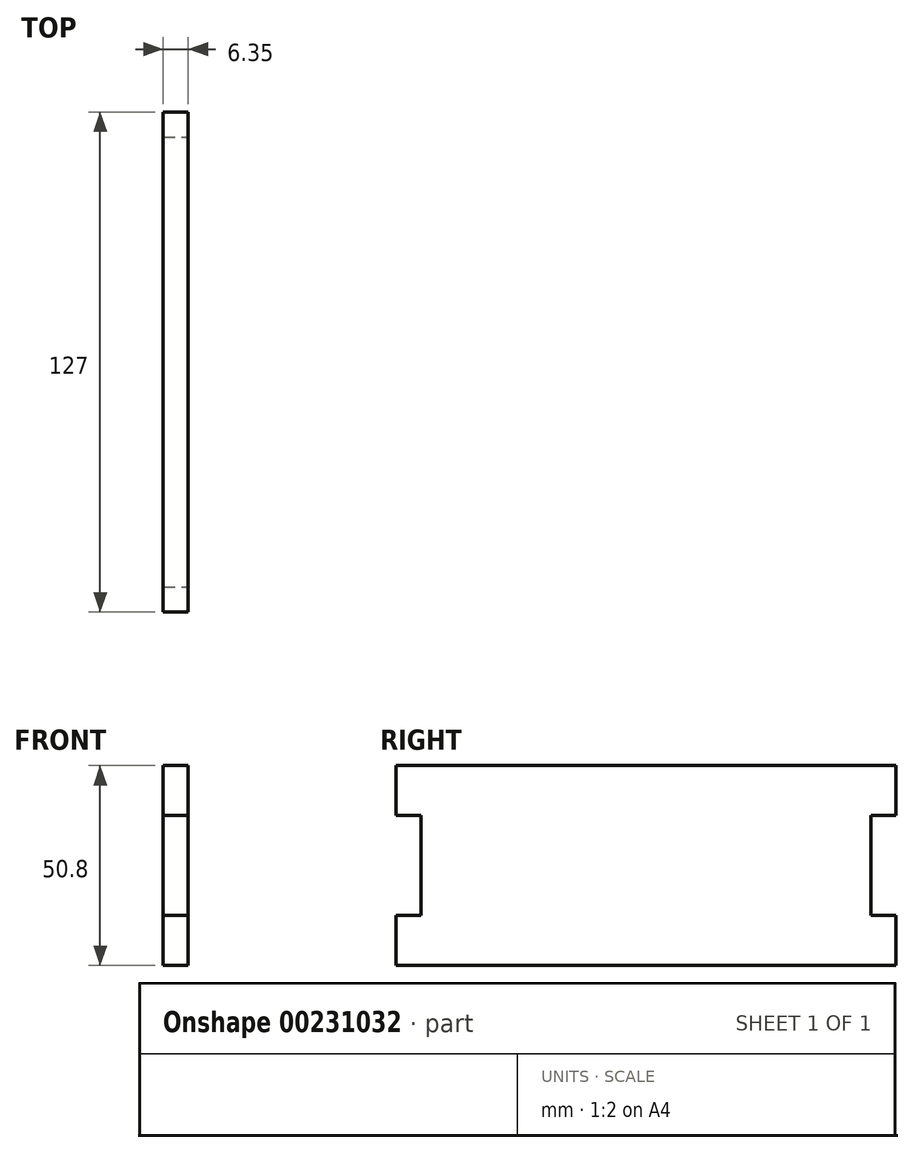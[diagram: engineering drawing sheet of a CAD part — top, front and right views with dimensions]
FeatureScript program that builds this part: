
annotation { "Feature Type Name" : "Feature", "Feature Type Description" : "" }
export const myFeature = defineFeature(function(context is Context, id is Id, definition is map)
    precondition{}
    {
        {
            var Q0;
            Q0=qCreatedBy(makeId("Right.planeOp"),FACE);
            var sketch = newSketch(context, id + "F0", { "sketchPlane" : qUnion([Q0])});
            skLineSegment(sketch, "E0.bottom", {"start": v(63.5, 25.4) * mm, "end": v(-63.5, 25.4) * mm});
            skLineSegment(sketch, "E0.top", {"start": v(63.5, -25.4) * mm, "end": v(-63.5, -25.4) * mm});
            skLineSegment(sketch, "E0.left", {"start": v(63.5, 25.4) * mm, "end": v(63.5, 12.7) * mm});
            skLineSegment(sketch, "E0.right", {"start": v(-63.5, 25.4) * mm, "end": v(-63.5, 12.7) * mm});
            skPoint(sketch, "E0.middle", {"position": v(0, 0) * mm});
            skLineSegment(sketch, "E1.bottom", {"start": v(-63.5, 25.4) * mm, "end": v(-57.15, 25.4) * mm});
            skLineSegment(sketch, "E1.top", {"start": v(-63.5, 19.05) * mm, "end": v(-57.15, 19.05) * mm});
            skLineSegment(sketch, "E1.left", {"start": v(-63.5, 25.4) * mm, "end": v(-63.5, 19.05) * mm});
            skLineSegment(sketch, "E1.right", {"start": v(-57.15, 25.4) * mm, "end": v(-57.15, 19.05) * mm});
            skLineSegment(sketch, "E2.top", {"start": v(-63.5, 12.7) * mm, "end": v(-57.15, 12.7) * mm});
            skLineSegment(sketch, "E2.left", {"start": v(-63.5, 19.05) * mm, "end": v(-63.5, 12.7) * mm});
            skLineSegment(sketch, "E2.right", {"start": v(-57.15, 19.05) * mm, "end": v(-57.15, 12.7) * mm});
            skLineSegment(sketch, "E3.bottom", {"start": v(-63.5, -19.05) * mm, "end": v(-57.15, -19.05) * mm});
            skLineSegment(sketch, "E3.top", {"start": v(-63.5, -25.4) * mm, "end": v(-57.15, -25.4) * mm});
            skLineSegment(sketch, "E3.left", {"start": v(-63.5, -19.05) * mm, "end": v(-63.5, -25.4) * mm});
            skLineSegment(sketch, "E3.right", {"start": v(-57.15, -19.05) * mm, "end": v(-57.15, -25.4) * mm});
            skLineSegment(sketch, "E4.bottom", {"start": v(-63.5, -12.7) * mm, "end": v(-57.15, -12.7) * mm});
            skLineSegment(sketch, "E4.left", {"start": v(-63.5, -12.7) * mm, "end": v(-63.5, -19.05) * mm});
            skLineSegment(sketch, "E4.right", {"start": v(-57.15, -12.7) * mm, "end": v(-57.15, -19.05) * mm});
            skLineSegment(sketch, "E5", {"start": v(-57.15, 12.7) * mm, "end": v(-57.15, -12.7) * mm});
            skLineSegment(sketch, "E6.trimOffspring", {"start": v(-63.5, -12.7) * mm, "end": v(-63.5, -25.4) * mm});
            skLineSegment(sketch, "E7.bottom", {"start": v(57.15, 25.4) * mm, "end": v(63.5, 25.4) * mm});
            skLineSegment(sketch, "E7.top", {"start": v(57.15, 19.05) * mm, "end": v(63.5, 19.05) * mm});
            skLineSegment(sketch, "E7.left", {"start": v(57.15, 25.4) * mm, "end": v(57.15, 19.05) * mm});
            skLineSegment(sketch, "E7.right", {"start": v(63.5, 25.4) * mm, "end": v(63.5, 19.05) * mm});
            skLineSegment(sketch, "E8.top", {"start": v(57.15, 12.7) * mm, "end": v(63.5, 12.7) * mm});
            skLineSegment(sketch, "E8.left", {"start": v(57.15, 19.05) * mm, "end": v(57.15, 12.7) * mm});
            skLineSegment(sketch, "E8.right", {"start": v(63.5, 19.05) * mm, "end": v(63.5, 12.7) * mm});
            skLineSegment(sketch, "E9.bottom", {"start": v(57.15, -12.7) * mm, "end": v(63.5, -12.7) * mm});
            skLineSegment(sketch, "E9.top", {"start": v(57.15, -19.05) * mm, "end": v(63.5, -19.05) * mm});
            skLineSegment(sketch, "E9.left", {"start": v(57.15, -12.7) * mm, "end": v(57.15, -19.05) * mm});
            skLineSegment(sketch, "E9.right", {"start": v(63.5, -12.7) * mm, "end": v(63.5, -19.05) * mm});
            skLineSegment(sketch, "E10.top", {"start": v(57.15, -25.4) * mm, "end": v(63.5, -25.4) * mm});
            skLineSegment(sketch, "E10.left", {"start": v(57.15, -19.05) * mm, "end": v(57.15, -25.4) * mm});
            skLineSegment(sketch, "E10.right", {"start": v(63.5, -19.05) * mm, "end": v(63.5, -25.4) * mm});
            skLineSegment(sketch, "E11", {"start": v(57.15, 12.7) * mm, "end": v(57.15, -12.7) * mm});
            skLineSegment(sketch, "E12.trimOffspring", {"start": v(63.5, -12.7) * mm, "end": v(63.5, -25.4) * mm});
            skSolve(sketch);
        }
        {
            var Q0;
            Q0 = qSketchRegion(id + "F0", true);
            extrude(context, id + "F1", {"entities" : qUnion([Q0]), "oppositeDirection" : true, "depth" : 6.35 * mm});
        }
    });
